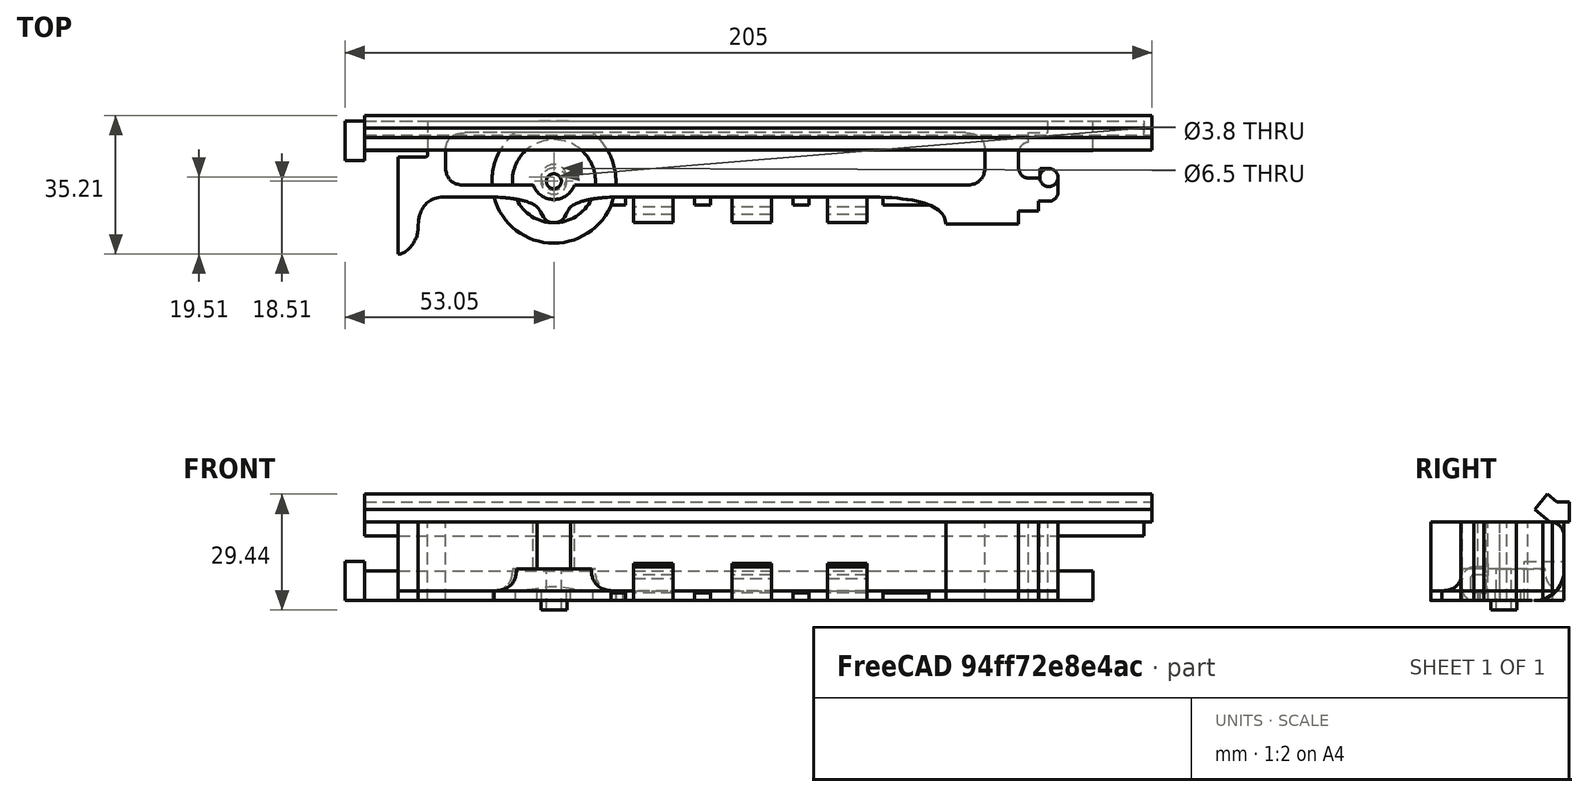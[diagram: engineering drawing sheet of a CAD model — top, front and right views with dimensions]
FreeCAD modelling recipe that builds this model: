
FCSTD DOCUMENT  (FreeCAD 0.19R0.19.2)
Label: v0_29
License: All rights reserved
LicenseURL: http://en.wikipedia.org/wiki/All_rights_reserved
objects: Part::Box×39, Part::MultiFuse×17, App::MeasureDistance×7, Sketcher::SketchObject×6, Part::Extrusion×5, Part::Cut×3, Part::Fillet×2, Part::Revolution×1, Mesh::Feature×1
note: 73 computed .brp shape members not serialized (recipe doc carries the construction recipe); baked Part::Feature solids carry a one-line shape summary decoded from their .brp

FEATURE [Sketcher::SketchObject] Sketch
  FullyConstrained = true
  sketch-geometry (66):
    g0: Circle CenterX=-101.95 CenterY=-14.3 CenterZ=0 NormalX=0 NormalY=0 NormalZ=1 AngleXU=0 Radius=3.25
    g1: LineSegment StartX=-134 StartY=2.59e-14 StartZ=0 EndX=-134 EndY=-8.6 EndZ=0
    g2: LineSegment StartX=-134.5 StartY=-9.1 StartZ=0 EndX=-141.5 EndY=-9.1 EndZ=0
    g3: ArcOfCircle CenterX=-134.5 CenterY=-8.6 CenterZ=0 NormalX=0 NormalY=0 NormalZ=1 AngleXU=0 Radius=0.5 StartAngle=4.71239 EndAngle=6.28319
    g4: Circle CenterX=-97.7 CenterY=-21.8 CenterZ=0 NormalX=0 NormalY=0 NormalZ=1 AngleXU=0 Radius=1
    g5: Circle CenterX=-94.45 CenterY=-19.3 CenterZ=0 NormalX=0 NormalY=0 NormalZ=1 AngleXU=0 Radius=1
    g6: Circle CenterX=-84.45 CenterY=-19.3 CenterZ=0 NormalX=0 NormalY=0 NormalZ=1 AngleXU=0 Radius=1
    g7: BSplineCurve PolesCount=3 KnotsCount=2 Degree=2 IsPeriodic=0
    g8: GeomPoint X=-97.7 Y=-21.8 Z=0
    g9: GeomPoint X=-84.45 Y=-19.3 Z=0
    g10: Circle CenterX=-106.2 CenterY=-21.8 CenterZ=0 NormalX=0 NormalY=0 NormalZ=1 AngleXU=0 Radius=1
    g11: Circle CenterX=-109.45 CenterY=-19.3 CenterZ=0 NormalX=0 NormalY=0 NormalZ=1 AngleXU=0 Radius=1
    g12: Circle CenterX=-119.45 CenterY=-19.3 CenterZ=0 NormalX=0 NormalY=0 NormalZ=1 AngleXU=0 Radius=1
    g13: BSplineCurve PolesCount=3 KnotsCount=2 Degree=2 IsPeriodic=0
    g14: GeomPoint X=-106.2 Y=-21.8 Z=0
    g15: GeomPoint X=-119.45 Y=-19.3 Z=0
    g16: LineSegment StartX=-141.5 StartY=-9.1 StartZ=0 EndX=-141.5 EndY=-33.8 EndZ=0
    g17-g20: Circle x4 (B-spline internal-alignment scaffolding for g21; pole/knot coordinates omitted)
    g21: BSplineCurve PolesCount=4 KnotsCount=2 Degree=3 IsPeriodic=0
    g22: GeomPoint X=-141.5 Y=-33.8 Z=0
    g23: GeomPoint X=-136.5 Y=-27.8 Z=0
    g24: Circle CenterX=-136.5 CenterY=-27.8 CenterZ=0 NormalX=0 NormalY=0 NormalZ=1 AngleXU=0 Radius=1
    g25: Circle CenterX=-136.5 CenterY=-19.3 CenterZ=0 NormalX=0 NormalY=0 NormalZ=1 AngleXU=0 Radius=1
    g26: Circle CenterX=-129.5 CenterY=-19.3 CenterZ=0 NormalX=0 NormalY=0 NormalZ=1 AngleXU=0 Radius=1
    g27: BSplineCurve PolesCount=3 KnotsCount=2 Degree=2 IsPeriodic=0
    g28: GeomPoint X=-136.5 Y=-27.8 Z=0
    g29: GeomPoint X=-129.5 Y=-19.3 Z=0
    g30: LineSegment StartX=-129.5 StartY=-19.3 StartZ=0 EndX=-119.45 EndY=-19.3 EndZ=0
    g31-g37: Circle x7 (B-spline internal-alignment scaffolding for g38; pole/knot coordinates omitted)
    g38: BSplineCurve PolesCount=7 KnotsCount=5 Degree=3 IsPeriodic=0
    g39-g43: GeomPoint x5 (B-spline internal-alignment scaffolding for g38; pole/knot coordinates omitted)
    g44: BSplineCurve PolesCount=3 KnotsCount=2 Degree=2 IsPeriodic=0
    g45: GeomPoint X=-2.4 Y=-26.2 Z=0
    g46: GeomPoint X=-22.4 Y=-19.3 Z=0
    g47: LineSegment StartX=-84.45 StartY=-19.3 StartZ=0 EndX=-22.4 EndY=-19.3 EndZ=0
    g48: LineSegment StartX=16.1 StartY=-26.2 StartZ=0 EndX=16.1 EndY=-22.9 EndZ=0
    g49: ArcOfCircle CenterX=23.8 CenterY=-14.35 CenterZ=0 NormalX=0 NormalY=0 NormalZ=1 AngleXU=0 Radius=2.3 StartAngle=8e-16 EndAngle=1.5708
    g50: LineSegment StartX=18.6 StartY=-5.40742 StartZ=0 EndX=18.6 EndY=-2.9 EndZ=0
    g51: LineSegment StartX=18.6 StartY=-2.9 StartZ=0 EndX=23.6 EndY=-2.9 EndZ=0
    g52: LineSegment StartX=23.6 StartY=-2.9 StartZ=0 EndX=23.6 EndY=2.58e-14 EndZ=0
    g53: LineSegment StartX=18.8 StartY=-14.55 StartZ=0 EndX=21.5 EndY=-14.55 EndZ=0
    g54: LineSegment StartX=21.5 StartY=-12.05 StartZ=0 EndX=21.5 EndY=-14.55 EndZ=0
    g55: LineSegment StartX=21.5 StartY=-12.05 StartZ=0 EndX=23.8 EndY=-12.05 EndZ=0
    g56: ArcOfCircle CenterX=23.8 CenterY=-18.1 CenterZ=0 NormalX=0 NormalY=0 NormalZ=1 AngleXU=0 Radius=2.3 StartAngle=4.71239 EndAngle=6.28319
    g57: LineSegment StartX=23.8 StartY=-20.4 StartZ=0 EndX=21.1 EndY=-20.4 EndZ=0
    g58: LineSegment StartX=26.1 StartY=-14.35 StartZ=0 EndX=26.1 EndY=-18.1 EndZ=0
    g59: ArcOfCircle CenterX=18.8 CenterY=-8.1 CenterZ=0 NormalX=0 NormalY=0 NormalZ=1 AngleXU=0 Radius=2.7 StartAngle=1.64494 EndAngle=3.14159
    g60: ArcOfCircle CenterX=18.8 CenterY=-11.85 CenterZ=0 NormalX=0 NormalY=0 NormalZ=1 AngleXU=0 Radius=2.7 StartAngle=3.14159 EndAngle=4.71239
    g61: LineSegment StartX=16.1 StartY=-8.1 StartZ=0 EndX=16.1 EndY=-11.85 EndZ=0
    g62: LineSegment StartX=21.1 StartY=-22.9 StartZ=0 EndX=21.1 EndY=-20.4 EndZ=0
    g63: LineSegment StartX=16.1 StartY=-22.9 StartZ=0 EndX=21.1 EndY=-22.9 EndZ=0
    g64: LineSegment StartX=-2.4 StartY=-26.2 StartZ=0 EndX=16.1 EndY=-26.2 EndZ=0
    g65: LineSegment StartX=23.6 StartY=2.59e-14 StartZ=0 EndX=-134 EndY=2.59e-14 EndZ=0
  constraints (103):
    c: Block(g0)
    c: Vertical(g1)
    c: Distance(g1) = 8.6
    c: Horizontal(g2)
    c: Distance(g2) = 7
    c: Coincident(g3,g1)
    c: Coincident(g3,g2)
    c: Block(g3)
    c: Weight(g4) = 1
    c: Equal(g4,g5)
    c: Equal(g4,g6)
    c: InternalAlignment(g4,g7)
    c: InternalAlignment(g5,g7)
    c: InternalAlignment(g6,g7)
    c: InternalAlignment(g8,g7)
    c: InternalAlignment(g9,g7)
    c: Weight(g10) = 1
    c: Equal(g10,g11)
    c: Equal(g10,g12)
    c: InternalAlignment(g10,g13)
    c: InternalAlignment(g11,g13)
    c: InternalAlignment(g12,g13)
    c: InternalAlignment(g14,g13)
    c: InternalAlignment(g15,g13)
    c: Block(g13)
    c: Block(g7)
    c: Coincident(g16,g2)
    c: Vertical(g16)
    c: Block(g16)
    c: Coincident(g21,g16)
    c: Weight(g17) = 1
    c: Equal(g17,g18)
    c: Equal(g17,g19)
    c: Equal(g17,g20)
    c: InternalAlignment(g17-g20 -> g21) x4
    c: InternalAlignment(g22,g21)
    c: InternalAlignment(g23,g21)
    c: Weight(g24) = 1
    c: Equal(g24,g25)
    c: Equal(g24,g26)
    c: InternalAlignment(g24,g27)
    c: InternalAlignment(g25,g27)
    c: InternalAlignment(g26,g27)
    c: InternalAlignment(g28,g27)
    c: InternalAlignment(g29,g27)
    c: Block(g21)
    c: Block(g27)
    c: Coincident(g30,g27)
    c: Coincident(g30,g13)
    c: Horizontal(g30)
    c: Weight(g31) = 1
    c: Equal(g31, g32-g37) x6
    c: InternalAlignment(g31-g37 -> g38) x7
    c: InternalAlignment(g39-g43 -> g38) x5
    c: Block(g38)
    c: InternalAlignment(g45,g44)
    c: InternalAlignment(g46,g44)
    c: Block(g44)
    c: Coincident(g47,g7)
    c: Coincident(g47,g44)
    c: Horizontal(g47)
    c: Vertical(g48)
    c: Distance(g48) = 3.3
    c: Block(g56)
    c: Block(g49)
    c: Coincident(g57,g56)
    c: Horizontal(g57)
    c: Vertical(g62)
    c: Coincident(g62,g57)
    c: Coincident(g58,g49)
    c: Coincident(g58,g56)
    c: Vertical(g58)
    c: Vertical(g50)
    c: Block(g50)
    c: Coincident(g51,g50)
    c: Horizontal(g51)
    c: Vertical(g52)
    c: Block(g52)
    c: Block(g51)
    c: Coincident(g59,g50)
    c: Block(g60)
    c: Coincident(g61,g59)
    c: Vertical(g61)
    c: Block(g61)
    c: Coincident(g53,g60)
    c: Horizontal(g53)
    c: Vertical(g54)
    c: Coincident(g54,g53)
    c: Block(g54)
    c: Coincident(g55,g49)
    c: Horizontal(g55)
    c: Block(g55)
    c: Coincident(g63,g62)
    c: Horizontal(g63)
    c: Block(g63)
    c: Block(g59)
    c: Coincident(g63,g48)
    c: Coincident(g64,g44)
    c: Coincident(g64,g48)
    c: Horizontal(g64)
    c: Coincident(g65,g52)
    c: Coincident(g65,g1)
    c: Horizontal(g65)
FEATURE [Part::Extrusion] Extrude
  Base = -> Sketch
  Dir = (0,0,1)
  DirMode = 2
  FaceMakerClass = Part::FaceMakerBullseye
  LengthFwd = 2.4
  LengthRev = 0
  Solid = true
  Symmetric = false
FEATURE [Sketcher::SketchObject] Sketch001
  FullyConstrained = true
  sketch-geometry (87):
    g0: LineSegment StartX=-134 StartY=0 StartZ=0 EndX=-134 EndY=-8.6 EndZ=0
    g1: LineSegment StartX=-134.5 StartY=-9.1 StartZ=0 EndX=-141.5 EndY=-9.1 EndZ=0
    g2: ArcOfCircle CenterX=-134.5 CenterY=-8.6 CenterZ=0 NormalX=0 NormalY=0 NormalZ=1 AngleXU=0 Radius=0.5 StartAngle=4.71239 EndAngle=6.28319
    g3: Circle CenterX=-97.7 CenterY=-21.8 CenterZ=0 NormalX=0 NormalY=0 NormalZ=1 AngleXU=0 Radius=1
    g4: Circle CenterX=-94.45 CenterY=-19.3 CenterZ=0 NormalX=0 NormalY=0 NormalZ=1 AngleXU=0 Radius=1
    g5: Circle CenterX=-84.45 CenterY=-19.3 CenterZ=0 NormalX=0 NormalY=0 NormalZ=1 AngleXU=0 Radius=1
    g6: BSplineCurve PolesCount=3 KnotsCount=2 Degree=2 IsPeriodic=0
    g7: GeomPoint X=-97.7 Y=-21.8 Z=0
    g8: GeomPoint X=-84.45 Y=-19.3 Z=0
    g9: Circle CenterX=-106.2 CenterY=-21.8 CenterZ=0 NormalX=0 NormalY=0 NormalZ=1 AngleXU=0 Radius=1
    g10: Circle CenterX=-109.45 CenterY=-19.3 CenterZ=0 NormalX=0 NormalY=0 NormalZ=1 AngleXU=0 Radius=1
    g11: Circle CenterX=-119.45 CenterY=-19.3 CenterZ=0 NormalX=0 NormalY=0 NormalZ=1 AngleXU=0 Radius=1
    g12: BSplineCurve PolesCount=3 KnotsCount=2 Degree=2 IsPeriodic=0
    g13: GeomPoint X=-106.2 Y=-21.8 Z=0
    g14: GeomPoint X=-119.45 Y=-19.3 Z=0
    g15: LineSegment StartX=-141.5 StartY=-9.1 StartZ=0 EndX=-141.5 EndY=-33.8 EndZ=0
    g16-g19: Circle x4 (B-spline internal-alignment scaffolding for g20; pole/knot coordinates omitted)
    g20: BSplineCurve PolesCount=4 KnotsCount=2 Degree=3 IsPeriodic=0
    g21: GeomPoint X=-141.5 Y=-33.8 Z=0
    g22: GeomPoint X=-136.5 Y=-27.8 Z=0
    g23: Circle CenterX=-136.5 CenterY=-27.8 CenterZ=0 NormalX=0 NormalY=0 NormalZ=1 AngleXU=0 Radius=1
    g24: Circle CenterX=-136.5 CenterY=-19.3 CenterZ=0 NormalX=0 NormalY=0 NormalZ=1 AngleXU=0 Radius=1
    g25: Circle CenterX=-129.5 CenterY=-19.3 CenterZ=0 NormalX=0 NormalY=0 NormalZ=1 AngleXU=0 Radius=1
    g26: BSplineCurve PolesCount=3 KnotsCount=2 Degree=2 IsPeriodic=0
    g27: GeomPoint X=-136.5 Y=-27.8 Z=0
    g28: GeomPoint X=-129.5 Y=-19.3 Z=0
    g29: LineSegment StartX=-129.5 StartY=-19.3 StartZ=0 EndX=-119.45 EndY=-19.3 EndZ=0
    g30-g36: Circle x7 (B-spline internal-alignment scaffolding for g37; pole/knot coordinates omitted)
    g37: BSplineCurve PolesCount=7 KnotsCount=5 Degree=3 IsPeriodic=0
    g38-g42: GeomPoint x5 (B-spline internal-alignment scaffolding for g37; pole/knot coordinates omitted)
    g43: Circle CenterX=-124.5 CenterY=-16.3 CenterZ=0 NormalX=0 NormalY=0 NormalZ=1 AngleXU=0 Radius=1
    g44: Circle CenterX=-129.5 CenterY=-16.3 CenterZ=0 NormalX=0 NormalY=0 NormalZ=1 AngleXU=0 Radius=1
    g45: Circle CenterX=-129.5 CenterY=-11.3 CenterZ=0 NormalX=0 NormalY=0 NormalZ=1 AngleXU=0 Radius=1
    g46: BSplineCurve PolesCount=3 KnotsCount=2 Degree=2 IsPeriodic=0
    g47: GeomPoint X=-124.5 Y=-16.3 Z=0
    g48: GeomPoint X=-129.5 Y=-11.3 Z=0
    g49: Circle CenterX=-129.5 CenterY=-8 CenterZ=0 NormalX=0 NormalY=0 NormalZ=1 AngleXU=0 Radius=1
    g50: Circle CenterX=-129.5 CenterY=-3 CenterZ=0 NormalX=0 NormalY=0 NormalZ=1 AngleXU=0 Radius=1
    g51: Circle CenterX=-124.5 CenterY=-3 CenterZ=0 NormalX=0 NormalY=0 NormalZ=1 AngleXU=0 Radius=1
    g52: BSplineCurve PolesCount=3 KnotsCount=2 Degree=2 IsPeriodic=0
    g53: GeomPoint X=-129.5 Y=-8 Z=0
    g54: GeomPoint X=-124.5 Y=-3 Z=0
    g55: LineSegment StartX=-129.5 StartY=-8 StartZ=0 EndX=-129.5 EndY=-11.3 EndZ=0
    g56: ArcOfCircle CenterX=-101.95 CenterY=-14.3 CenterZ=0 NormalX=0 NormalY=0 NormalZ=1 AngleXU=0 Radius=5.61805 StartAngle=3.50557 EndAngle=5.91921
    g57: LineSegment StartX=-124.5 StartY=-16.3 StartZ=0 EndX=-107.2 EndY=-16.3 EndZ=0
    g58: Circle CenterX=-2.4 CenterY=-26.2 CenterZ=0 NormalX=0 NormalY=0 NormalZ=1 AngleXU=0 Radius=1
    g59: Circle CenterX=-2.4 CenterY=-19.3 CenterZ=0 NormalX=0 NormalY=0 NormalZ=1 AngleXU=0 Radius=1
    g60: Circle CenterX=-22.4 CenterY=-19.3 CenterZ=0 NormalX=0 NormalY=0 NormalZ=1 AngleXU=0 Radius=1
    g61: BSplineCurve PolesCount=3 KnotsCount=2 Degree=2 IsPeriodic=0
    g62: GeomPoint X=-2.4 Y=-26.2 Z=0
    g63: LineSegment StartX=-22.4 StartY=-19.3 StartZ=0 EndX=-84.45 EndY=-19.3 EndZ=0
    g64: LineSegment StartX=18.6 StartY=-2.9 StartZ=0 EndX=23.6 EndY=-2.9 EndZ=0
    g65: ArcOfCircle CenterX=23.8 CenterY=-14.35 CenterZ=0 NormalX=0 NormalY=0 NormalZ=1 AngleXU=0 Radius=2.3 StartAngle=8e-16 EndAngle=1.5708
    g66: ArcOfCircle CenterX=23.8 CenterY=-18.1 CenterZ=0 NormalX=0 NormalY=0 NormalZ=1 AngleXU=0 Radius=2.3 StartAngle=4.71239 EndAngle=6.28319
    g67: LineSegment StartX=23.8 StartY=-20.4 StartZ=0 EndX=21.1 EndY=-20.4 EndZ=0
    g68: LineSegment StartX=21.1 StartY=-22.9 StartZ=0 EndX=21.1 EndY=-20.4 EndZ=0
    g69: LineSegment StartX=26.1 StartY=-14.35 StartZ=0 EndX=26.1 EndY=-18.1 EndZ=0
    g70: LineSegment StartX=18.6 StartY=-5.40742 StartZ=0 EndX=18.6 EndY=-2.9 EndZ=0
    g71: ArcOfCircle CenterX=18.8 CenterY=-8.1 CenterZ=0 NormalX=0 NormalY=0 NormalZ=1 AngleXU=0 Radius=2.7 StartAngle=1.64494 EndAngle=3.14159
    g72: ArcOfCircle CenterX=18.8 CenterY=-11.85 CenterZ=0 NormalX=0 NormalY=0 NormalZ=1 AngleXU=0 Radius=2.7 StartAngle=3.14159 EndAngle=4.71239
    g73: LineSegment StartX=16.1 StartY=-8.1 StartZ=0 EndX=16.1 EndY=-11.85 EndZ=0
    g74: LineSegment StartX=18.8 StartY=-14.55 StartZ=0 EndX=21.5 EndY=-14.55 EndZ=0
    g75: LineSegment StartX=21.5 StartY=-12.05 StartZ=0 EndX=21.5 EndY=-14.55 EndZ=0
    g76: LineSegment StartX=21.5 StartY=-12.05 StartZ=0 EndX=23.8 EndY=-12.05 EndZ=0
    g77: LineSegment StartX=16.1 StartY=-22.9 StartZ=0 EndX=21.1 EndY=-22.9 EndZ=0
    g78: LineSegment StartX=23.6 StartY=-2.9 StartZ=0 EndX=23.6 EndY=0 EndZ=0
    g79: LineSegment StartX=16.1 StartY=-22.9 StartZ=0 EndX=16.1 EndY=-26.2 EndZ=0
    g80: LineSegment StartX=-2.4 StartY=-26.2 StartZ=0 EndX=16.1 EndY=-26.2 EndZ=0
    g81: LineSegment StartX=-134 StartY=0 StartZ=0 EndX=23.6 EndY=0 EndZ=0
    g82: BSplineCurve PolesCount=3 KnotsCount=2 Degree=2 IsPeriodic=0
    g83: LineSegment StartX=7.6 StartY=-8 StartZ=0 EndX=7.6 EndY=-11.3 EndZ=0
    g84: BSplineCurve PolesCount=3 KnotsCount=2 Degree=2 IsPeriodic=0
    g85: LineSegment StartX=2.6 StartY=-16.3 StartZ=0 EndX=-96.7 EndY=-16.3 EndZ=0
    g86: LineSegment StartX=2.6 StartY=-3 StartZ=0 EndX=-124.5 EndY=-3 EndZ=0
  constraints (141):
    c: Vertical(g0)
    c: Distance(g0) = 8.6
    c: Horizontal(g1)
    c: Distance(g1) = 7
    c: Coincident(g2,g0)
    c: Coincident(g2,g1)
    c: Block(g2)
    c: Weight(g3) = 1
    c: Equal(g3,g4)
    c: Equal(g3,g5)
    c: InternalAlignment(g3,g6)
    c: InternalAlignment(g4,g6)
    c: InternalAlignment(g5,g6)
    c: InternalAlignment(g7,g6)
    c: InternalAlignment(g8,g6)
    c: Weight(g9) = 1
    c: Equal(g9,g10)
    c: Equal(g9,g11)
    c: InternalAlignment(g9,g12)
    c: InternalAlignment(g10,g12)
    c: InternalAlignment(g11,g12)
    c: InternalAlignment(g13,g12)
    c: InternalAlignment(g14,g12)
    c: Block(g6)
    c: Coincident(g15,g1)
    c: Vertical(g15)
    c: Block(g15)
    c: Coincident(g20,g15)
    c: Weight(g16) = 1
    c: Equal(g16,g17)
    c: Equal(g16,g18)
    c: Equal(g16,g19)
    c: InternalAlignment(g16-g19 -> g20) x4
    c: InternalAlignment(g21,g20)
    c: InternalAlignment(g22,g20)
    c: Weight(g23) = 1
    c: Equal(g23,g24)
    c: Equal(g23,g25)
    c: InternalAlignment(g23,g26)
    c: InternalAlignment(g24,g26)
    c: InternalAlignment(g25,g26)
    c: InternalAlignment(g27,g26)
    c: InternalAlignment(g28,g26)
    c: Block(g20)
    c: Coincident(g29,g26)
    c: Coincident(g29,g12)
    c: Horizontal(g29)
    c: Weight(g30) = 1
    c: Equal(g30, g31-g36) x6
    c: InternalAlignment(g30-g36 -> g37) x7
    c: InternalAlignment(g38-g42 -> g37) x5
    c: Block(g37)
    c: Block(g12)
    c: Block(g26)
    c: Weight(g43) = 1
    c: Equal(g43,g44)
    c: Equal(g43,g45)
    c: InternalAlignment(g43,g46)
    c: InternalAlignment(g44,g46)
    c: InternalAlignment(g45,g46)
    c: InternalAlignment(g47,g46)
    c: InternalAlignment(g48,g46)
    c: Weight(g49) = 1
    c: Equal(g49,g50)
    c: Equal(g49,g51)
    c: InternalAlignment(g49,g52)
    c: InternalAlignment(g50,g52)
    c: InternalAlignment(g51,g52)
    c: InternalAlignment(g53,g52)
    c: InternalAlignment(g54,g52)
    c: Block(g52)
    c: Block(g46)
    c: Coincident(g55,g52)
    c: Coincident(g55,g46)
    c: Vertical(g55)
    c: Coincident(g57,g46)
    c: Coincident(g57,g56)
    c: Horizontal(g57)
    c: Block(g56)
    c: Equal(g58,g59)
    c: Equal(g58,g60)
    c: InternalAlignment(g58,g61)
    c: InternalAlignment(g59,g61)
    c: InternalAlignment(g60,g61)
    c: InternalAlignment(g62,g61)
    c: Block(g61)
    c: Coincident(g63,g61)
    c: Coincident(g63,g6)
    c: Horizontal(g63)
    c: Block(g63)
    c: Block(g66)
    c: Block(g65)
    c: Coincident(g67,g66)
    c: Horizontal(g67)
    c: Vertical(g68)
    c: Coincident(g68,g67)
    c: Coincident(g69,g65)
    c: Coincident(g69,g66)
    c: Vertical(g69)
    c: Vertical(g70)
    c: Block(g70)
    c: Coincident(g64,g70)
    c: Horizontal(g64)
    c: Block(g64)
    c: Coincident(g71,g70)
    c: Block(g72)
    c: Vertical(g73)
    c: Block(g73)
    c: Coincident(g74,g72)
    c: Horizontal(g74)
    c: Vertical(g75)
    c: Coincident(g75,g74)
    c: Block(g75)
    c: Coincident(g76,g65)
    c: Horizontal(g76)
    c: Block(g76)
    c: Coincident(g77,g68)
    c: Horizontal(g77)
    c: Block(g77)
    c: Block(g71)
    c: Coincident(g78,g64)
    c: Vertical(g78)
    c: Vertical(g79)
    c: Block(g79)
    c: Coincident(g80,g61)
    c: Coincident(g80,g79)
    c: Horizontal(g80)
    c: Coincident(g81,g0)
    c: Horizontal(g81)
    c: Coincident(g81,g78)
    c: Block(g82)
    c: Block(g84)
    c: Coincident(g83,g84)
    c: Coincident(g83,g82)
    c: Vertical(g83)
    c: Coincident(g85,g82)
    c: Coincident(g85,g56)
    c: Horizontal(g85)
    c: Coincident(g86,g84)
    c: Coincident(g86,g52)
    c: Horizontal(g86)
FEATURE [Part::Extrusion] Extrude001
  Base = -> Sketch001
  Dir = (0,0,1)
  DirMode = 2
  FaceMakerClass = Part::FaceMakerBullseye
  LengthFwd = 20
  LengthRev = 0
  Solid = true
  Symmetric = false
FEATURE [Sketcher::SketchObject] Sketch004
  FullyConstrained = true
  Placement = pos=(0,0,0) rot=(1,0,0;1.5708rad)
  sketch-geometry (12):
    g0: LineSegment StartX=15.75 StartY=2.5 StartZ=0 EndX=15.75 EndY=0 EndZ=0
    g1: Circle CenterX=15.75 CenterY=2.5 CenterZ=0 NormalX=0 NormalY=0 NormalZ=1 AngleXU=0 Radius=1
    g2: Circle CenterX=10.55 CenterY=2.5 CenterZ=0 NormalX=0 NormalY=0 NormalZ=1 AngleXU=0 Radius=1
    g3: Circle CenterX=10.55 CenterY=8 CenterZ=0 NormalX=0 NormalY=0 NormalZ=1 AngleXU=0 Radius=1
    g4: BSplineCurve PolesCount=3 KnotsCount=2 Degree=2 IsPeriodic=0
    g5: GeomPoint X=15.75 Y=2.5 Z=0
    g6: GeomPoint X=10.55 Y=8 Z=0
    g7: LineSegment StartX=1.9 StartY=8 StartZ=0 EndX=10.55 EndY=8 EndZ=0
    g8: LineSegment StartX=1.9 StartY=-2.4 StartZ=0 EndX=1.9 EndY=8 EndZ=0
    g9: LineSegment StartX=3.30092 StartY=-2.4 StartZ=0 EndX=3.30092 EndY=0 EndZ=0
    g10: LineSegment StartX=15.75 StartY=0 StartZ=0 EndX=3.30092 EndY=0 EndZ=0
    g11: LineSegment StartX=3.30092 StartY=-2.4 StartZ=0 EndX=1.9 EndY=-2.4 EndZ=0
  constraints (26):
    c: Vertical(g0)
    c: Distance(g0) = 2.5
    c: Coincident(g4,g0)
    c: Weight(g1) = 1
    c: Equal(g1,g2)
    c: Equal(g1,g3)
    c: InternalAlignment(g1,g4)
    c: InternalAlignment(g2,g4)
    c: InternalAlignment(g3,g4)
    c: InternalAlignment(g5,g4)
    c: InternalAlignment(g6,g4)
    c: Block(g4)
    c: Coincident(g7,g4)
    c: Horizontal(g7)
    c: Vertical(g8)
    c: Coincident(g8,g7)
    c: Block(g8)
    c: Vertical(g9)
    c: Coincident(g10,g0)
    c: PointOnObject(g10,g-1)
    c: Horizontal(g10)
    c: Coincident(g10,g9)
    c: Block(g9)
    c: Coincident(g11,g9)
    c: Coincident(g11,g8)
    c: Horizontal(g11)
FEATURE [Part::Revolution] Revolve  label="mainScrewStandRevolve"
  Angle = 360
  Axis = (0,0,1)
  Base = (0,0,0)
  FaceMakerClass = Part::FaceMakerBullseye
  Placement = pos=(-101.95,-15.3,0) rot=(0,0,1;0rad)
  Solid = true
  Source = -> Sketch004
  Symmetric = false
FEATURE [Sketcher::SketchObject] Sketch044
  FullyConstrained = true
  MapMode = 4
  Placement = pos=(0,0,0) rot=(0.57735,0.57735,0.57735;2.0944rad)
  sketch-geometry (14):
    g0: LineSegment StartX=6.08745 StartY=-4.11588 StartZ=0 EndX=6.08745 EndY=-2.11589 EndZ=0
    g1: LineSegment StartX=8.08745 StartY=1.38411 StartZ=0 EndX=8.08745 EndY=-1.11589 EndZ=0
    g2: ArcOfCircle CenterX=7.08745 CenterY=-1.11589 CenterZ=0 NormalX=0 NormalY=0 NormalZ=1 AngleXU=0 Radius=1 StartAngle=4.71239 EndAngle=6.28319
    g3: LineSegment StartX=6.08745 StartY=-2.11589 StartZ=0 EndX=7.08745 EndY=-2.11589 EndZ=0
    g4: LineSegment StartX=6.08745 StartY=-4.11588 StartZ=0 EndX=7.08745 EndY=-4.11588 EndZ=0
    g5: ArcOfCircle CenterX=7.08745 CenterY=-1.11589 CenterZ=0 NormalX=0 NormalY=0 NormalZ=1 AngleXU=0 Radius=3 StartAngle=4.71239 EndAngle=6.28319
    g6: ArcOfCircle CenterX=7.08745 CenterY=1.38411 CenterZ=0 NormalX=0 NormalY=0 NormalZ=1 AngleXU=0 Radius=1 StartAngle=5.35e-14 EndAngle=1.5708
    g7: LineSegment StartX=10.0875 StartY=-1.11588 StartZ=0 EndX=10.0875 EndY=1.38411 EndZ=0
    g8: ArcOfCircle CenterX=7.08745 CenterY=1.38411 CenterZ=0 NormalX=0 NormalY=0 NormalZ=1 AngleXU=0 Radius=3 StartAngle=3.57e-14 EndAngle=1.5708
    g9: ArcOfCircle CenterX=4.58745 CenterY=1.38412 CenterZ=0 NormalX=0 NormalY=0 NormalZ=1 AngleXU=0 Radius=1 StartAngle=1.57081 EndAngle=3.14159
    g10: LineSegment StartX=4.58744 StartY=2.38411 StartZ=0 EndX=7.08745 EndY=2.38411 EndZ=0
    g11: LineSegment StartX=4.58745 StartY=4.38411 StartZ=0 EndX=7.08745 EndY=4.38411 EndZ=0
    g12: ArcOfCircle CenterX=4.58745 CenterY=5.38411 CenterZ=0 NormalX=0 NormalY=0 NormalZ=1 AngleXU=0 Radius=1 StartAngle=3.14159 EndAngle=4.71239
    g13: LineSegment StartX=3.58745 StartY=5.38411 StartZ=0 EndX=3.58745 EndY=1.38411 EndZ=0
  constraints (33):
    c: Vertical(g0)
    c: Block(g0)
    c: Block(g1)
    c: Coincident(g2,g1)
    c: Coincident(g3,g0)
    c: Coincident(g3,g2)
    c: Horizontal(g3)
    c: Block(g2)
    c: Coincident(g4,g0)
    c: Horizontal(g4)
    c: Coincident(g5,g2)
    c: Block(g5)
    c: Block(g4)
    c: Coincident(g6,g1)
    c: Block(g6)
    c: Coincident(g7,g5)
    c: Vertical(g7)
    c: Coincident(g8,g6)
    c: Block(g8)
    c: Block(g7)
    c: Coincident(g10,g9)
    c: Coincident(g10,g6)
    c: Horizontal(g10)
    c: Block(g10)
    c: Block(g9)
    c: Coincident(g11,g8)
    c: Horizontal(g11)
    c: Block(g12)
    c: Block(g11)
    c: Coincident(g13,g12)
    c: Coincident(g13,g9)
    c: Vertical(g13)
    c: Tangent(g13,g9)
FEATURE [Part::Extrusion] Extrude039
  Base = -> Sketch044
  Dir = (1,0,0)
  DirMode = 2
  FaceMakerClass = Part::FaceMakerBullseye
  LengthFwd = 10
  LengthRev = 0
  Placement = pos=(-46.7,-15.71,4.115) rot=(0,0,1;3.14159rad)
  Solid = true
  Symmetric = false
FEATURE [Sketcher::SketchObject] Sketch045
  FullyConstrained = true
  MapMode = 4
  Placement = pos=(0,0,0) rot=(0.57735,0.57735,0.57735;2.0944rad)
  sketch-geometry (14):
    g0: LineSegment StartX=6.08745 StartY=-4.11588 StartZ=0 EndX=6.08745 EndY=-2.11589 EndZ=0
    g1: LineSegment StartX=8.08745 StartY=1.38411 StartZ=0 EndX=8.08745 EndY=-1.11589 EndZ=0
    g2: ArcOfCircle CenterX=7.08745 CenterY=-1.11589 CenterZ=0 NormalX=0 NormalY=0 NormalZ=1 AngleXU=0 Radius=1 StartAngle=4.71239 EndAngle=6.28319
    g3: LineSegment StartX=6.08745 StartY=-2.11589 StartZ=0 EndX=7.08745 EndY=-2.11589 EndZ=0
    g4: LineSegment StartX=6.08745 StartY=-4.11588 StartZ=0 EndX=7.08745 EndY=-4.11588 EndZ=0
    g5: ArcOfCircle CenterX=7.08745 CenterY=-1.11589 CenterZ=0 NormalX=0 NormalY=0 NormalZ=1 AngleXU=0 Radius=3 StartAngle=4.71239 EndAngle=6.28319
    g6: ArcOfCircle CenterX=7.08745 CenterY=1.38411 CenterZ=0 NormalX=0 NormalY=0 NormalZ=1 AngleXU=0 Radius=1 StartAngle=5.35e-14 EndAngle=1.5708
    g7: LineSegment StartX=10.0875 StartY=-1.11588 StartZ=0 EndX=10.0875 EndY=1.38411 EndZ=0
    g8: ArcOfCircle CenterX=7.08745 CenterY=1.38411 CenterZ=0 NormalX=0 NormalY=0 NormalZ=1 AngleXU=0 Radius=3 StartAngle=3.57e-14 EndAngle=1.5708
    g9: ArcOfCircle CenterX=4.58745 CenterY=1.38412 CenterZ=0 NormalX=0 NormalY=0 NormalZ=1 AngleXU=0 Radius=1 StartAngle=1.57081 EndAngle=3.14159
    g10: LineSegment StartX=4.58744 StartY=2.38411 StartZ=0 EndX=7.08745 EndY=2.38411 EndZ=0
    g11: LineSegment StartX=4.58745 StartY=4.38411 StartZ=0 EndX=7.08745 EndY=4.38411 EndZ=0
    g12: ArcOfCircle CenterX=4.58745 CenterY=5.38411 CenterZ=0 NormalX=0 NormalY=0 NormalZ=1 AngleXU=0 Radius=1 StartAngle=3.14159 EndAngle=4.71239
    g13: LineSegment StartX=3.58745 StartY=5.38411 StartZ=0 EndX=3.58745 EndY=1.38411 EndZ=0
  constraints (33):
    c: Vertical(g0)
    c: Block(g0)
    c: Block(g1)
    c: Coincident(g2,g1)
    c: Coincident(g3,g0)
    c: Coincident(g3,g2)
    c: Horizontal(g3)
    c: Block(g2)
    c: Coincident(g4,g0)
    c: Horizontal(g4)
    c: Coincident(g5,g2)
    c: Block(g5)
    c: Block(g4)
    c: Coincident(g6,g1)
    c: Block(g6)
    c: Coincident(g7,g5)
    c: Vertical(g7)
    c: Coincident(g8,g6)
    c: Block(g8)
    c: Block(g7)
    c: Coincident(g10,g9)
    c: Coincident(g10,g6)
    c: Horizontal(g10)
    c: Block(g10)
    c: Block(g9)
    c: Coincident(g11,g8)
    c: Horizontal(g11)
    c: Block(g12)
    c: Block(g11)
    c: Coincident(g13,g12)
    c: Coincident(g13,g9)
    c: Vertical(g13)
    c: Tangent(g13,g9)
FEATURE [Part::Extrusion] Extrude040
  Base = -> Sketch045
  Dir = (1,0,0)
  DirMode = 2
  FaceMakerClass = Part::FaceMakerBullseye
  LengthFwd = 10
  LengthRev = 0
  Placement = pos=(-71.7,-15.71,4.115) rot=(0,0,1;3.14159rad)
  Solid = true
  Symmetric = false
FEATURE [Part::Box] Box017  label="Cube017"
  AttacherType = Attacher::AttachEngine3D
  Height = 2
  Length = 2
  Placement = pos=(-85.7,-21.3,0) rot=(0,0,1;0rad)
  Width = 2
FEATURE [App::MeasureDistance] Distance  label="Distance: 6.80 mm"
  Distance = 6.80017
  P1 = (-83.7,-21.2887,0)
  P2 = (-81.7,-21.35,6.49911)
FEATURE [App::MeasureDistance] Distance001  label="Distance: 6.80 mm001"
  Distance = 6.80051
  P1 = (-69.7,-21.2829,0)
  P2 = (-71.7,-21.3744,6.49911)
FEATURE [Part::Box] Box018  label="Cube018"
  AttacherType = Attacher::AttachEngine3D
  Height = 2
  Length = 2
  Placement = pos=(-87.7,-21.3,0) rot=(0,0,1;0rad)
  Width = 2
FEATURE [Part::MultiFuse] Fusion
  Shapes = -> [Box017,Box018]
FEATURE [Part::Box] Box019  label="Cube019"
  AttacherType = Attacher::AttachEngine3D
  Height = 2
  Length = 2
  Placement = pos=(-85.7,-21.3,0) rot=(0,0,1;0rad)
  Width = 2
FEATURE [Part::Box] Box020  label="Cube020"
  AttacherType = Attacher::AttachEngine3D
  Height = 2
  Length = 2
  Placement = pos=(-87.7,-21.3,0) rot=(0,0,1;0rad)
  Width = 2
FEATURE [App::MeasureDistance] Distance002  label="Distance: 2.07 mm"
  Distance = 2.06534
  P1 = (-67.7,-21.2821,0)
  P2 = (-65.7,-21.7975,-0.00088501)
FEATURE [App::MeasureDistance] Distance003  label="Distance: 2.08 mm"
  Distance = 2.0829
  P1 = (-55.7,-21.7975,-0.00088501)
  P2 = (-53.682,-21.2816,0)
FEATURE [Part::Box] Box021  label="Cube021"
  AttacherType = Attacher::AttachEngine3D
  Height = 2
  Length = 2
  Placement = pos=(-85.7,-21.3,0) rot=(0,0,1;0rad)
  Width = 2
FEATURE [Part::Box] Box022  label="Cube022"
  AttacherType = Attacher::AttachEngine3D
  Height = 2
  Length = 2
  Placement = pos=(-87.7,-21.3,0) rot=(0,0,1;0rad)
  Width = 2
FEATURE [Part::Box] Box023  label="Cube023"
  AttacherType = Attacher::AttachEngine3D
  Height = 2
  Length = 2
  Placement = pos=(-85.7,-21.3,0) rot=(0,0,1;0rad)
  Width = 2
FEATURE [Part::Box] Box024  label="Cube024"
  AttacherType = Attacher::AttachEngine3D
  Height = 2
  Length = 2
  Placement = pos=(-87.7,-21.3,0) rot=(0,0,1;0rad)
  Width = 2
FEATURE [Part::Box] Box025  label="Cube025"
  AttacherType = Attacher::AttachEngine3D
  Height = 2
  Length = 2
  Placement = pos=(-85.7,-21.3,0) rot=(0,0,1;0rad)
  Width = 2
FEATURE [Part::Box] Box026  label="Cube026"
  AttacherType = Attacher::AttachEngine3D
  Height = 2
  Length = 2
  Placement = pos=(-87.7,-21.3,0) rot=(0,0,1;0rad)
  Width = 2
FEATURE [Part::Box] Box  label="Cube"
  AttacherType = Attacher::AttachEngine3D
  Height = 10
  Length = 10
  Placement = pos=(-107,0,0) rot=(0,0,1;0rad)
  Width = 10
FEATURE [Sketcher::SketchObject] Sketch046
  FullyConstrained = true
  MapMode = 4
  Placement = pos=(0,0,0) rot=(0.57735,0.57735,0.57735;2.0944rad)
  sketch-geometry (14):
    g0: LineSegment StartX=6.08745 StartY=-4.11588 StartZ=0 EndX=6.08745 EndY=-2.11589 EndZ=0
    g1: LineSegment StartX=8.08745 StartY=1.38411 StartZ=0 EndX=8.08745 EndY=-1.11589 EndZ=0
    g2: ArcOfCircle CenterX=7.08745 CenterY=-1.11589 CenterZ=0 NormalX=0 NormalY=0 NormalZ=1 AngleXU=0 Radius=1 StartAngle=4.71239 EndAngle=6.28319
    g3: LineSegment StartX=6.08745 StartY=-2.11589 StartZ=0 EndX=7.08745 EndY=-2.11589 EndZ=0
    g4: LineSegment StartX=6.08745 StartY=-4.11588 StartZ=0 EndX=7.08745 EndY=-4.11588 EndZ=0
    g5: ArcOfCircle CenterX=7.08745 CenterY=-1.11589 CenterZ=0 NormalX=0 NormalY=0 NormalZ=1 AngleXU=0 Radius=3 StartAngle=4.71239 EndAngle=6.28319
    g6: ArcOfCircle CenterX=7.08745 CenterY=1.38411 CenterZ=0 NormalX=0 NormalY=0 NormalZ=1 AngleXU=0 Radius=1 StartAngle=5.35e-14 EndAngle=1.5708
    g7: LineSegment StartX=10.0875 StartY=-1.11588 StartZ=0 EndX=10.0875 EndY=1.38411 EndZ=0
    g8: ArcOfCircle CenterX=7.08745 CenterY=1.38411 CenterZ=0 NormalX=0 NormalY=0 NormalZ=1 AngleXU=0 Radius=3 StartAngle=3.57e-14 EndAngle=1.5708
    g9: ArcOfCircle CenterX=4.58745 CenterY=1.38412 CenterZ=0 NormalX=0 NormalY=0 NormalZ=1 AngleXU=0 Radius=1 StartAngle=1.57081 EndAngle=3.14159
    g10: LineSegment StartX=4.58744 StartY=2.38411 StartZ=0 EndX=7.08745 EndY=2.38411 EndZ=0
    g11: LineSegment StartX=4.58745 StartY=4.38411 StartZ=0 EndX=7.08745 EndY=4.38411 EndZ=0
    g12: ArcOfCircle CenterX=4.58745 CenterY=5.38411 CenterZ=0 NormalX=0 NormalY=0 NormalZ=1 AngleXU=0 Radius=1 StartAngle=3.14159 EndAngle=4.71239
    g13: LineSegment StartX=3.58745 StartY=5.38411 StartZ=0 EndX=3.58745 EndY=1.38411 EndZ=0
  constraints (33):
    c: Vertical(g0)
    c: Block(g0)
    c: Block(g1)
    c: Coincident(g2,g1)
    c: Coincident(g3,g0)
    c: Coincident(g3,g2)
    c: Horizontal(g3)
    c: Block(g2)
    c: Coincident(g4,g0)
    c: Horizontal(g4)
    c: Coincident(g5,g2)
    c: Block(g5)
    c: Block(g4)
    c: Coincident(g6,g1)
    c: Block(g6)
    c: Coincident(g7,g5)
    c: Vertical(g7)
    c: Coincident(g8,g6)
    c: Block(g8)
    c: Block(g7)
    c: Coincident(g10,g9)
    c: Coincident(g10,g6)
    c: Horizontal(g10)
    c: Block(g10)
    c: Block(g9)
    c: Coincident(g11,g8)
    c: Horizontal(g11)
    c: Block(g12)
    c: Block(g11)
    c: Coincident(g13,g12)
    c: Coincident(g13,g9)
    c: Vertical(g13)
    c: Tangent(g13,g9)
FEATURE [Part::Extrusion] Extrude041
  Base = -> Sketch046
  Dir = (1,0,0)
  DirMode = 2
  FaceMakerClass = Part::FaceMakerBullseye
  LengthFwd = 10
  LengthRev = 0
  Placement = pos=(-22.4,-15.71,4.115) rot=(0,0,1;3.14159rad)
  Solid = true
  Symmetric = false
FEATURE [Part::Box] Box027  label="Cube027"
  AttacherType = Attacher::AttachEngine3D
  Height = 2
  Length = 2
  Placement = pos=(-85.7,-21.3,0) rot=(0,0,1;0rad)
  Width = 2
FEATURE [Part::Box] Box028  label="Cube028"
  AttacherType = Attacher::AttachEngine3D
  Height = 2
  Length = 2
  Placement = pos=(-87.7,-21.3,0) rot=(0,0,1;0rad)
  Width = 2
FEATURE [Part::MultiFuse] Fusion009
  Placement = pos=(21.5,0,0) rot=(0,0,1;0rad)
  Shapes = -> [Box027,Box028]
FEATURE [Part::Box] Box029  label="Cube029"
  AttacherType = Attacher::AttachEngine3D
  Height = 2
  Length = 2
  Placement = pos=(-87.7,-21.3,0) rot=(0,0,1;0rad)
  Width = 2
FEATURE [Part::Box] Box030  label="Cube030"
  AttacherType = Attacher::AttachEngine3D
  Height = 2
  Length = 2
  Placement = pos=(-85.7,-21.3,0) rot=(0,0,1;0rad)
  Width = 2
FEATURE [Part::MultiFuse] Fusion010
  Shapes = -> [Box030,Box029]
FEATURE [Part::Box] Box032  label="Cube032"
  AttacherType = Attacher::AttachEngine3D
  Height = 2
  Length = 2
  Placement = pos=(-85.7,-21.3,0) rot=(0,0,1;0rad)
  Width = 2
FEATURE [Part::Box] Box033  label="Cube033"
  AttacherType = Attacher::AttachEngine3D
  Height = 2
  Length = 2
  Placement = pos=(-87.7,-21.3,0) rot=(0,0,1;0rad)
  Width = 2
FEATURE [Part::MultiFuse] Fusion011
  Shapes = -> [Box032,Box033]
FEATURE [Part::Box] Box034  label="Cube034"
  AttacherType = Attacher::AttachEngine3D
  Height = 2
  Length = 2
  Placement = pos=(-85.7,-21.3,0) rot=(0,0,1;0rad)
  Width = 2
FEATURE [Part::Box] Box035  label="Cube035"
  AttacherType = Attacher::AttachEngine3D
  Height = 2
  Length = 2
  Placement = pos=(-87.7,-21.3,0) rot=(0,0,1;0rad)
  Width = 2
FEATURE [Part::Box] Box036  label="Cube036"
  AttacherType = Attacher::AttachEngine3D
  Height = 2
  Length = 2
  Placement = pos=(-85.7,-21.3,0) rot=(0,0,1;0rad)
  Width = 2
FEATURE [Part::Box] Box037  label="Cube037"
  AttacherType = Attacher::AttachEngine3D
  Height = 2
  Length = 2
  Placement = pos=(-87.7,-21.3,0) rot=(0,0,1;0rad)
  Width = 2
FEATURE [Part::Box] Box038  label="Cube038"
  AttacherType = Attacher::AttachEngine3D
  Height = 2
  Length = 2
  Placement = pos=(-85.7,-21.3,0) rot=(0,0,1;0rad)
  Width = 2
FEATURE [Part::Box] Box039  label="Cube039"
  AttacherType = Attacher::AttachEngine3D
  Height = 2
  Length = 2
  Placement = pos=(-87.7,-21.3,0) rot=(0,0,1;0rad)
  Width = 2
FEATURE [Part::Box] Box040  label="Cube040"
  AttacherType = Attacher::AttachEngine3D
  Height = 2
  Length = 2
  Placement = pos=(-85.7,-21.3,0) rot=(0,0,1;0rad)
  Width = 2
FEATURE [Part::Box] Box041  label="Cube041"
  AttacherType = Attacher::AttachEngine3D
  Height = 2
  Length = 2
  Placement = pos=(-87.7,-21.3,0) rot=(0,0,1;0rad)
  Width = 2
FEATURE [App::MeasureDistance] Distance004  label="Distance: 15.00 mm"
  Distance = 15
  P1 = (-71.7,-25.7975,5.49911)
  P2 = (-56.7,-25.7975,5.49911)
FEATURE [Part::Box] Box042  label="Cube042"
  AttacherType = Attacher::AttachEngine3D
  Height = 2
  Length = 2
  Placement = pos=(-87.7,-21.3,0) rot=(0,0,1;0rad)
  Width = 2
FEATURE [Part::Box] Box043  label="Cube043"
  AttacherType = Attacher::AttachEngine3D
  Height = 2
  Length = 2
  Placement = pos=(-85.7,-21.3,0) rot=(0,0,1;0rad)
  Width = 2
FEATURE [Part::MultiFuse] Fusion019
  Placement = pos=(46.5,0,0) rot=(0,0,1;0rad)
  Shapes = -> [Box043,Box042]
FEATURE [Part::Box] Box044  label="Cube044"
  AttacherType = Attacher::AttachEngine3D
  Height = 2
  Length = 2
  Placement = pos=(-87.7,-21.3,0) rot=(0,0,1;0rad)
  Width = 2
FEATURE [Part::Box] Box045  label="Cube045"
  AttacherType = Attacher::AttachEngine3D
  Height = 2
  Length = 2
  Placement = pos=(-85.7,-21.3,0) rot=(0,0,1;0rad)
  Width = 2
FEATURE [Part::MultiFuse] Fusion020
  Placement = pos=(69.3,0,0) rot=(0,0,1;0rad)
  Shapes = -> [Box045,Box044]
FEATURE [App::MeasureDistance] Distance005  label="Distance: 8.08 mm"
  Distance = 8.08079
  P1 = (-37.2,-21.2879,0)
  P2 = (-32.4,-21.432,6.49911)
FEATURE [App::MeasureDistance] Distance006  label="Distance: 4.86 mm"
  Distance = 4.86199
  P1 = (-32.4,-21.7975,-0.00088501)
  P2 = (-37.2365,-21.3,0)
FEATURE [Part::Box] Box046  label="Cube046"
  AttacherType = Attacher::AttachEngine3D
  Height = 2
  Length = 2
  Placement = pos=(-87.7,-21.3,0) rot=(0,0,1;0rad)
  Width = 2
FEATURE [Part::Box] Box047  label="Cube047"
  AttacherType = Attacher::AttachEngine3D
  Height = 2
  Length = 2
  Placement = pos=(-85.7,-21.3,0) rot=(0,0,1;0rad)
  Width = 2
FEATURE [Part::MultiFuse] Fusion021
  Placement = pos=(73.3,0,0) rot=(0,0,1;0rad)
  Shapes = -> [Box047,Box046]
FEATURE [Part::Box] Box048  label="Cube048"
  AttacherType = Attacher::AttachEngine3D
  Height = 2
  Length = 2
  Placement = pos=(-87.7,-21.3,0) rot=(0,0,1;0rad)
  Width = 2
FEATURE [Part::Box] Box049  label="Cube049"
  AttacherType = Attacher::AttachEngine3D
  Height = 2
  Length = 2
  Placement = pos=(-85.7,-21.3,0) rot=(0,0,1;0rad)
  Width = 2
FEATURE [Part::MultiFuse] Fusion022
  Placement = pos=(77.3,0,0) rot=(0,0,1;0rad)
  Shapes = -> [Box049,Box048]
FEATURE [Part::MultiFuse] Fusion023
  Shapes = -> [Extrude001,Extrude040,Extrude039,Extrude041,Fusion020,Fusion019,Fusion009,Box025,Fusion021,Fusion022]
FEATURE [Part::MultiFuse] Fusion024
  Shapes = -> [Box034,Box035,Box036,Box037,Box038,Box039,Box040,Box041]
FEATURE [Part::MultiFuse] Fusion025
  Shapes = -> [Box021,Box022,Box023,Box024,Box026]
FEATURE [Part::MultiFuse] Fusion026
  Shapes = -> [Fusion023,Revolve]
FEATURE [Part::MultiFuse] Fusion027
  Shapes = -> [Fusion024,Fusion025,Fusion026]
FEATURE [Part::MultiFuse] Fusion028
  Shapes = -> [Fusion011,Fusion010,Fusion027]
FEATURE [Part::MultiFuse] Fusion029
  Shapes = -> [Fusion011,Fusion010,Fusion027,Box020,Box019,Fusion028]
FEATURE [Part::MultiFuse] Fusion030
  Shapes = -> [Fusion011,Fusion010,Fusion027,Box020,Box019,Fusion028,Fusion,Fusion029]
FEATURE [Part::Cut] Cut
  Base = -> Fusion030
  Tool = -> Box
FEATURE [Mesh::Feature] v0_28
FEATURE [Part::Box] Box005  label="Cube005"
  AttacherType = Attacher::AttachEngine3D
  Height = 10
  Length = 198
  Placement = pos=(-30,0,0) rot=(0,0,1;0rad)
  Width = 10
FEATURE [Part::Box] Box006  label="Cube006"
  AttacherType = Attacher::AttachEngine3D
  Height = 5
  Length = 200
  Placement = pos=(-30,6.4,10) rot=(1,0,0;0rad)
  Width = 5
FEATURE [Part::Box] Box007  label="Cube007"
  AttacherType = Attacher::AttachEngine3D
  Height = 5
  Length = 200
  Placement = pos=(-30,6.4,10) rot=(1,0,0;0.872665rad)
  Width = 5
FEATURE [Part::Box] Box004  label="Cube004"
  AttacherType = Attacher::AttachEngine3D
  Height = 10
  Length = 200
  Placement = pos=(-30,0,0) rot=(0,0,1;0rad)
  Width = 10
FEATURE [Part::Fillet] Fillet020
  Base = -> Box004
  Edges = 1 edges r=3.6: [Edge12]
FEATURE [Part::Cut] Cut012
  Base = -> Box005
  Tool = -> Fillet020
FEATURE [Part::MultiFuse] Fusion013  label="removeFromMainFusion013"
  Placement = pos=(-120,-10,10) rot=(0,0,1;0rad)
  Shapes = -> [Box007,Box006,Cut012]
FEATURE [Part::Box] Box050  label="Cube050"
  AttacherType = Attacher::AttachEngine3D
  Height = 10
  Length = 190
  Placement = pos=(-30,0,0) rot=(0,0,1;0rad)
  Width = 10
FEATURE [Part::Box] Box001  label="Cube001"
  AttacherType = Attacher::AttachEngine3D
  Height = 10
  Length = 190
  Placement = pos=(-35,0,0) rot=(0,0,1;0rad)
  Width = 10
FEATURE [Part::Fillet] Fillet008
  Base = -> Box050
  Edges = 1 edges r=7.5: [Edge11]
FEATURE [Part::Cut] Cut013  label="filletMain"
  Base = -> Box001
  Placement = pos=(-120,-10,0) rot=(0,0,1;0rad)
  Tool = -> Fillet008
